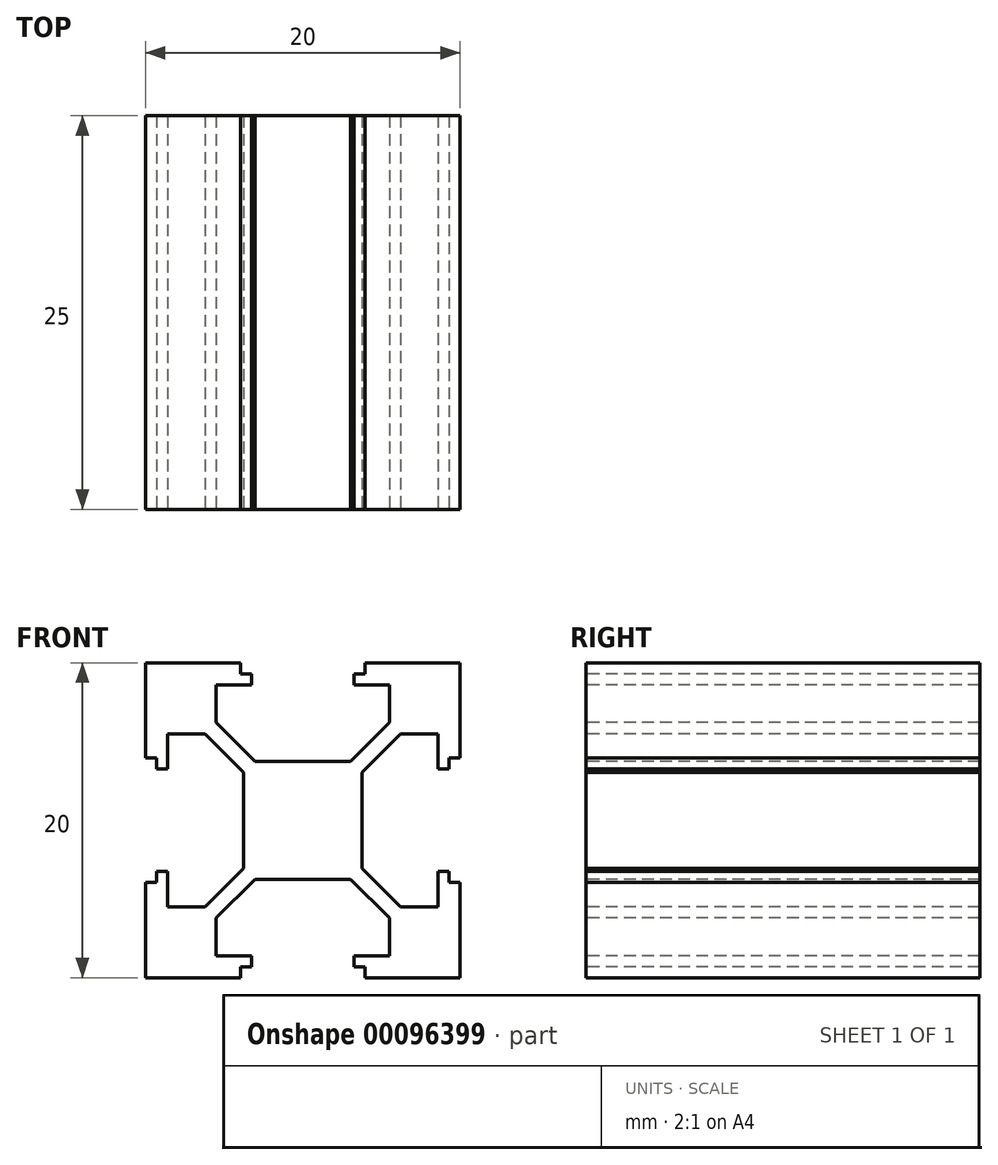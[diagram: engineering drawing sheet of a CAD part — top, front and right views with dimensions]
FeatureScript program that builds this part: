
annotation { "Feature Type Name" : "Feature", "Feature Type Description" : "" }
export const myFeature = defineFeature(function(context is Context, id is Id, definition is map)
    precondition{}
    {
        {
            var Q0;
            Q0=qCreatedBy(makeId("Front.planeOp"),FACE);
            var sketch = newSketch(context, id + "F0", { "sketchPlane" : qUnion([Q0])});
            skLineSegment(sketch, "E0.bottom", {"start": v(0, 0) * mm, "end": v(10, 0) * mm, "construction": true});
            skLineSegment(sketch, "E0.top", {"start": v(0, 10) * mm, "end": v(10, 10) * mm, "construction": true});
            skLineSegment(sketch, "E0.left", {"start": v(0, 0) * mm, "end": v(0, 10) * mm, "construction": true});
            skLineSegment(sketch, "E0.right", {"start": v(10, 0) * mm, "end": v(10, 10) * mm, "construction": true});
            skLineSegment(sketch, "E1", {"start": v(0, 0) * mm, "end": v(10, 10) * mm, "construction": true});
            skLineSegment(sketch, "E2", {"start": v(10, 10) * mm, "end": v(10, 3.95) * mm});
            skLineSegment(sketch, "E3", {"start": v(10, 3.95) * mm, "end": v(9.3, 3.95) * mm});
            skLineSegment(sketch, "E4", {"start": v(9.3, 3.95) * mm, "end": v(9.3, 3.25) * mm});
            skLineSegment(sketch, "E5", {"start": v(9.3, 3.25) * mm, "end": v(8.6, 3.25) * mm});
            skLineSegment(sketch, "E6", {"start": v(8.6, 3.25) * mm, "end": v(8.6, 5.5) * mm});
            skLineSegment(sketch, "E7", {"start": v(8.6, 5.5) * mm, "end": v(6.2, 5.5) * mm});
            skLineSegment(sketch, "E8", {"start": v(6.2, 5.5) * mm, "end": v(3.75, 3.04) * mm});
            skLineSegment(sketch, "E9", {"start": v(3.75, 3.04) * mm, "end": v(3.75, 0) * mm});
            skLineSegment(sketch, "E10.MirrorCS", {"start": v(3.04, 3.75) * mm, "end": v(0, 3.75) * mm});
            skLineSegment(sketch, "E11.MirrorCS", {"start": v(3.95, 10) * mm, "end": v(3.95, 9.3) * mm});
            skLineSegment(sketch, "E12.MirrorCS", {"start": v(3.25, 9.3) * mm, "end": v(3.25, 8.6) * mm});
            skLineSegment(sketch, "E13.MirrorCS", {"start": v(3.95, 9.3) * mm, "end": v(3.25, 9.3) * mm});
            skLineSegment(sketch, "E14.MirrorCS", {"start": v(3.25, 8.6) * mm, "end": v(5.5, 8.6) * mm});
            skLineSegment(sketch, "E15.MirrorCS", {"start": v(5.5, 6.2) * mm, "end": v(3.04, 3.75) * mm});
            skLineSegment(sketch, "E16.MirrorCS", {"start": v(5.5, 8.6) * mm, "end": v(5.5, 6.2) * mm});
            skLineSegment(sketch, "E17.MirrorCS", {"start": v(10, 10) * mm, "end": v(3.95, 10) * mm});
            skLineSegment(sketch, "E18.1.0", {"start": v(-6.2, 5.5) * mm, "end": v(-3.75, 3.04) * mm});
            skLineSegment(sketch, "E18.1.1", {"start": v(-8.6, 3.25) * mm, "end": v(-8.6, 5.5) * mm});
            skLineSegment(sketch, "E18.1.2", {"start": v(-10, 10) * mm, "end": v(-3.95, 10) * mm});
            skLineSegment(sketch, "E18.1.3", {"start": v(-8.6, 5.5) * mm, "end": v(-6.2, 5.5) * mm});
            skLineSegment(sketch, "E18.1.4", {"start": v(-3.25, 8.6) * mm, "end": v(-5.5, 8.6) * mm});
            skLineSegment(sketch, "E18.1.5", {"start": v(-5.5, 8.6) * mm, "end": v(-5.5, 6.2) * mm});
            skLineSegment(sketch, "E18.1.6", {"start": v(-10, 10) * mm, "end": v(-10, 3.95) * mm});
            skLineSegment(sketch, "E18.1.7", {"start": v(-5.5, 6.2) * mm, "end": v(-3.04, 3.75) * mm});
            skLineSegment(sketch, "E18.1.8", {"start": v(-9.3, 3.95) * mm, "end": v(-9.3, 3.25) * mm});
            skLineSegment(sketch, "E18.1.9", {"start": v(-9.3, 3.25) * mm, "end": v(-8.6, 3.25) * mm});
            skLineSegment(sketch, "E18.1.10", {"start": v(-10, 3.95) * mm, "end": v(-9.3, 3.95) * mm});
            skLineSegment(sketch, "E18.1.11", {"start": v(-3.95, 9.3) * mm, "end": v(-3.25, 9.3) * mm});
            skLineSegment(sketch, "E18.1.12", {"start": v(-3.25, 9.3) * mm, "end": v(-3.25, 8.6) * mm});
            skLineSegment(sketch, "E18.1.13", {"start": v(-3.95, 10) * mm, "end": v(-3.95, 9.3) * mm});
            skLineSegment(sketch, "E18.1.14", {"start": v(-3.75, 3.04) * mm, "end": v(-3.75, 0) * mm});
            skLineSegment(sketch, "E18.1.15", {"start": v(-3.04, 3.75) * mm, "end": v(0, 3.75) * mm});
            skLineSegment(sketch, "E18.2.0", {"start": v(-5.5, -6.2) * mm, "end": v(-3.04, -3.75) * mm});
            skLineSegment(sketch, "E18.2.1", {"start": v(-3.25, -8.6) * mm, "end": v(-5.5, -8.6) * mm});
            skLineSegment(sketch, "E18.2.2", {"start": v(-10, -10) * mm, "end": v(-10, -3.95) * mm});
            skLineSegment(sketch, "E18.2.3", {"start": v(-5.5, -8.6) * mm, "end": v(-5.5, -6.2) * mm});
            skLineSegment(sketch, "E18.2.4", {"start": v(-8.6, -3.25) * mm, "end": v(-8.6, -5.5) * mm});
            skLineSegment(sketch, "E18.2.5", {"start": v(-8.6, -5.5) * mm, "end": v(-6.2, -5.5) * mm});
            skLineSegment(sketch, "E18.2.6", {"start": v(-10, -10) * mm, "end": v(-3.95, -10) * mm});
            skLineSegment(sketch, "E18.2.7", {"start": v(-6.2, -5.5) * mm, "end": v(-3.75, -3.04) * mm});
            skLineSegment(sketch, "E18.2.8", {"start": v(-3.95, -9.3) * mm, "end": v(-3.25, -9.3) * mm});
            skLineSegment(sketch, "E18.2.9", {"start": v(-3.25, -9.3) * mm, "end": v(-3.25, -8.6) * mm});
            skLineSegment(sketch, "E18.2.10", {"start": v(-3.95, -10) * mm, "end": v(-3.95, -9.3) * mm});
            skLineSegment(sketch, "E18.2.11", {"start": v(-9.3, -3.95) * mm, "end": v(-9.3, -3.25) * mm});
            skLineSegment(sketch, "E18.2.12", {"start": v(-9.3, -3.25) * mm, "end": v(-8.6, -3.25) * mm});
            skLineSegment(sketch, "E18.2.13", {"start": v(-10, -3.95) * mm, "end": v(-9.3, -3.95) * mm});
            skLineSegment(sketch, "E18.2.14", {"start": v(-3.04, -3.75) * mm, "end": v(0, -3.75) * mm});
            skLineSegment(sketch, "E18.2.15", {"start": v(-3.75, -3.04) * mm, "end": v(-3.75, 0) * mm});
            skLineSegment(sketch, "E18.3.0", {"start": v(6.2, -5.5) * mm, "end": v(3.75, -3.04) * mm});
            skLineSegment(sketch, "E18.3.1", {"start": v(8.6, -3.25) * mm, "end": v(8.6, -5.5) * mm});
            skLineSegment(sketch, "E18.3.2", {"start": v(10, -10) * mm, "end": v(3.95, -10) * mm});
            skLineSegment(sketch, "E18.3.3", {"start": v(8.6, -5.5) * mm, "end": v(6.2, -5.5) * mm});
            skLineSegment(sketch, "E18.3.4", {"start": v(3.25, -8.6) * mm, "end": v(5.5, -8.6) * mm});
            skLineSegment(sketch, "E18.3.5", {"start": v(5.5, -8.6) * mm, "end": v(5.5, -6.2) * mm});
            skLineSegment(sketch, "E18.3.6", {"start": v(10, -10) * mm, "end": v(10, -3.95) * mm});
            skLineSegment(sketch, "E18.3.7", {"start": v(5.5, -6.2) * mm, "end": v(3.04, -3.75) * mm});
            skLineSegment(sketch, "E18.3.8", {"start": v(9.3, -3.95) * mm, "end": v(9.3, -3.25) * mm});
            skLineSegment(sketch, "E18.3.9", {"start": v(9.3, -3.25) * mm, "end": v(8.6, -3.25) * mm});
            skLineSegment(sketch, "E18.3.10", {"start": v(10, -3.95) * mm, "end": v(9.3, -3.95) * mm});
            skLineSegment(sketch, "E18.3.11", {"start": v(3.95, -9.3) * mm, "end": v(3.25, -9.3) * mm});
            skLineSegment(sketch, "E18.3.12", {"start": v(3.25, -9.3) * mm, "end": v(3.25, -8.6) * mm});
            skLineSegment(sketch, "E18.3.13", {"start": v(3.95, -10) * mm, "end": v(3.95, -9.3) * mm});
            skLineSegment(sketch, "E18.3.14", {"start": v(3.75, -3.04) * mm, "end": v(3.75, 0) * mm});
            skLineSegment(sketch, "E18.3.15", {"start": v(3.04, -3.75) * mm, "end": v(0, -3.75) * mm});
            skPoint(sketch, "E18.center", {"position": v(0, 0) * mm});
            skSolve(sketch);
        }
        {
            var Q0;
            Q0=makeQuery(id+"F0.imprint","IMPRINT",FACE,{"disambiguationData":[TD([[makeQuery(id+"F0.imprint","IMPRINT",EDGE,{"derivedFrom":sQuery(id+"F0.wireOp",EDGE,"E2")}),-1.0]])]});
            extrude(context, id + "F1", {"entities" : qUnion([Q0]), "oppositeDirection" : true, "depth" : 25 * mm});
        }
    });
